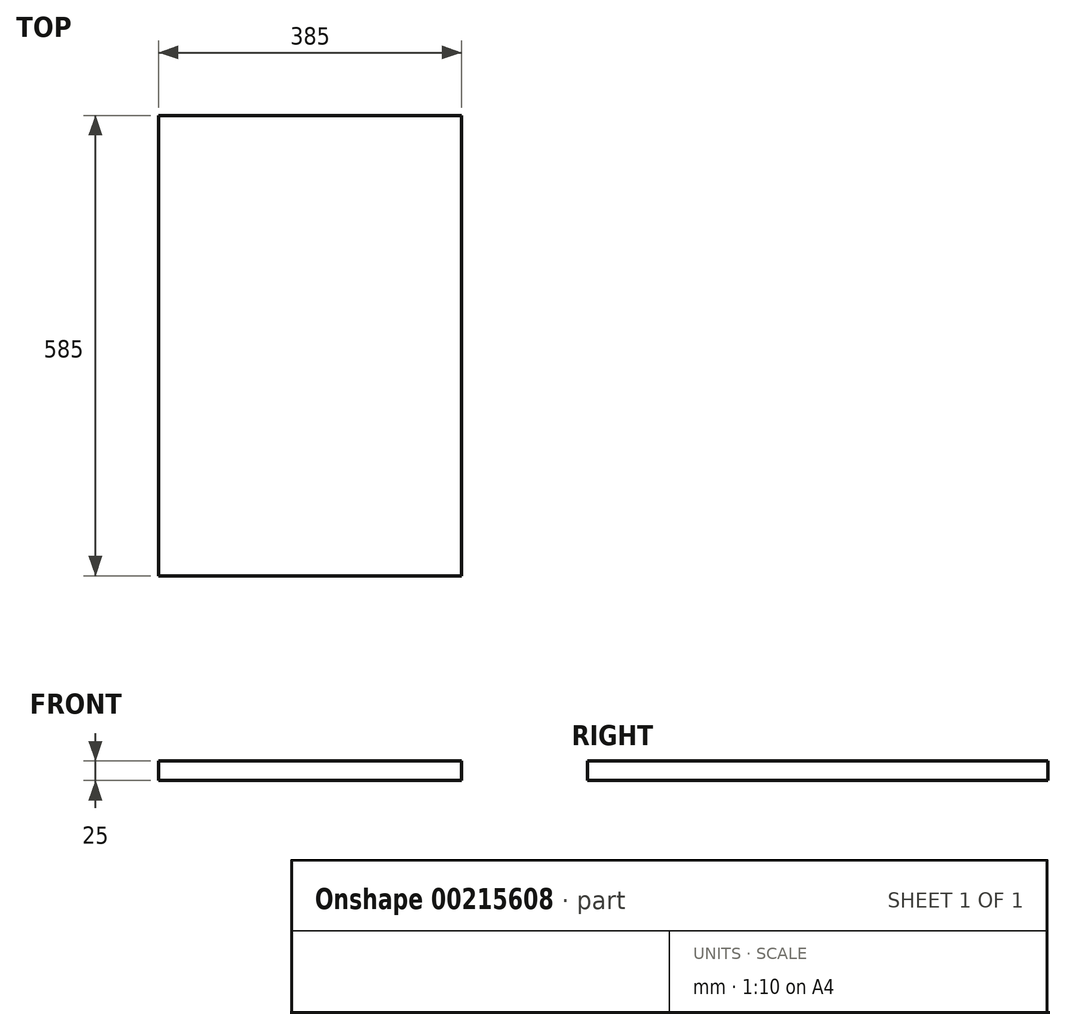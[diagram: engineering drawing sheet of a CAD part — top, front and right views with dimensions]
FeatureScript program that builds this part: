
annotation { "Feature Type Name" : "Feature", "Feature Type Description" : "" }
export const myFeature = defineFeature(function(context is Context, id is Id, definition is map)
    precondition{}
    {
        {
            var Q0;
            Q0=qCreatedBy(makeId("Top.planeOp"),FACE);
            var sketch = newSketch(context, id + "F0", { "sketchPlane" : qUnion([Q0])});
            skLineSegment(sketch, "E0.bottom", {"start": v(-189.66, 292.5) * mm, "end": v(195.34, 292.5) * mm});
            skLineSegment(sketch, "E0.top", {"start": v(-189.66, -292.5) * mm, "end": v(195.34, -292.5) * mm});
            skLineSegment(sketch, "E0.left", {"start": v(-189.66, 292.5) * mm, "end": v(-189.66, -292.5) * mm});
            skLineSegment(sketch, "E0.right", {"start": v(195.34, 292.5) * mm, "end": v(195.34, -292.5) * mm});
            skPoint(sketch, "E0.middle", {"position": v(2.84, 0) * mm});
            skSolve(sketch);
        }
        {
            var Q0;
            Q0 = qSketchRegion(id + "F0", true);
            extrude(context, id + "F1", {"entities" : qUnion([Q0]), "endBound" : BoundingType.SYMMETRIC, "depth" : 25 * mm});
        }
    });
